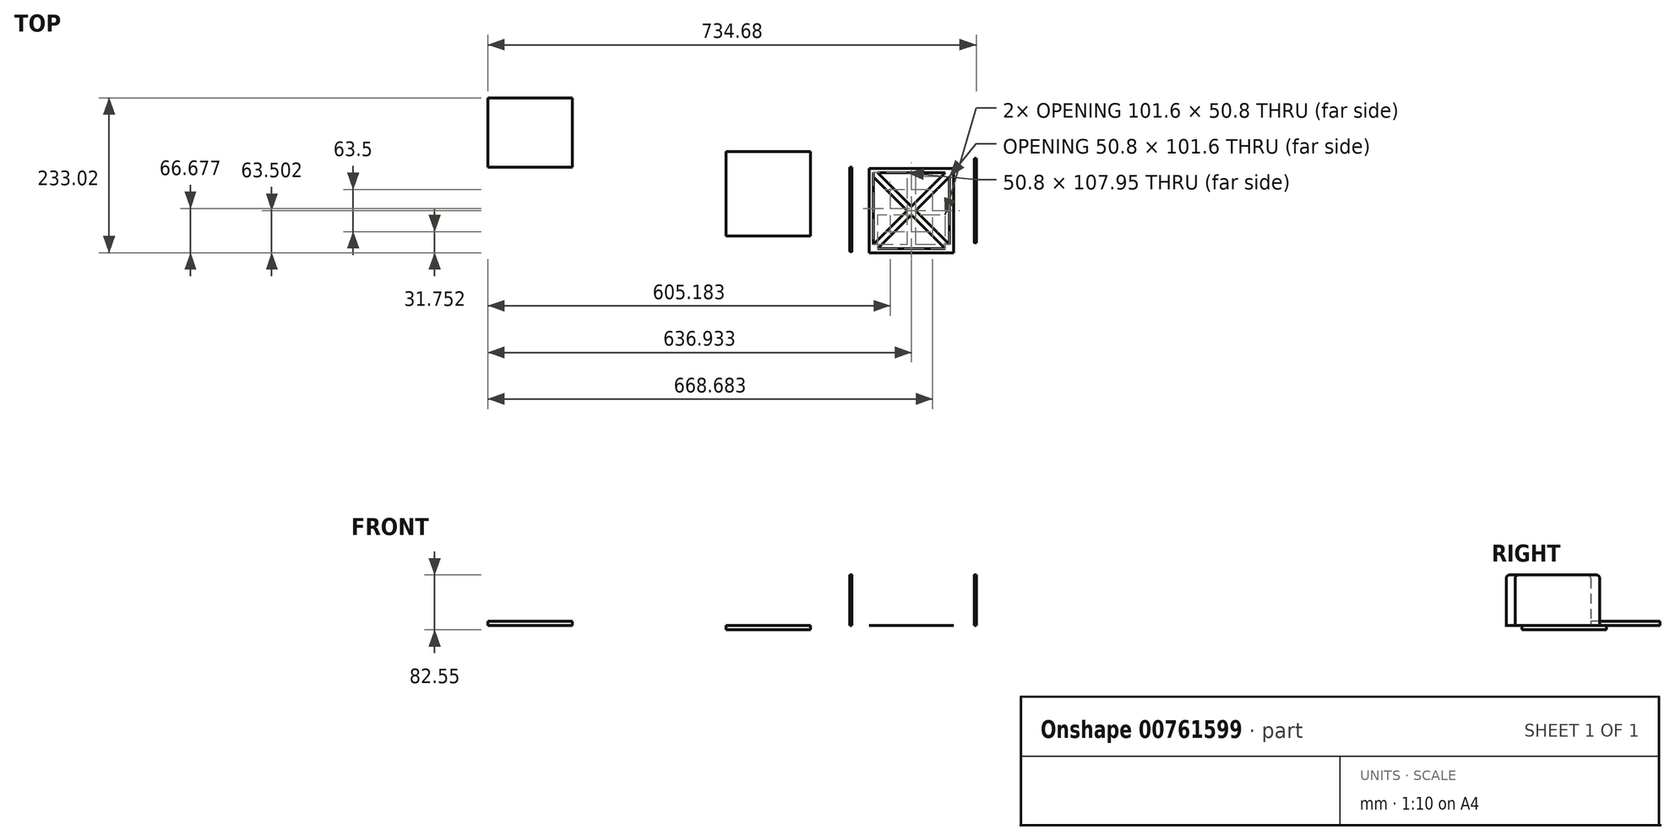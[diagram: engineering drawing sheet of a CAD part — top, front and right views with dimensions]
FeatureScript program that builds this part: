
annotation { "Feature Type Name" : "Feature", "Feature Type Description" : "" }
export const myFeature = defineFeature(function(context is Context, id is Id, definition is map)
    precondition{}
    {
        {
            var Q0;
            Q0=qCreatedBy(makeId("Top.planeOp"),FACE);
            var sketch = newSketch(context, id + "F0", { "sketchPlane" : qUnion([Q0])});
            skLineSegment(sketch, "E0.bottom", {"start": v(-34.56, 29.71) * mm, "end": v(79.74, 29.71) * mm});
            skLineSegment(sketch, "E0.top", {"start": v(-34.56, -84.59) * mm, "end": v(79.74, -84.59) * mm});
            skLineSegment(sketch, "E0.left", {"start": v(-34.56, 29.71) * mm, "end": v(-34.56, -84.59) * mm});
            skLineSegment(sketch, "E0.right", {"start": v(79.74, 29.71) * mm, "end": v(79.74, -84.59) * mm});
            skLineSegment(sketch, "E1.bottom", {"start": v(79.74, 29.71) * mm, "end": v(79.74, 29.71) * mm});
            skLineSegment(sketch, "E1.top", {"start": v(79.74, -84.59) * mm, "end": v(79.74, -84.59) * mm});
            skLineSegment(sketch, "E2.bottom", {"start": v(79.74, 29.71) * mm, "end": v(86.1, 29.71) * mm});
            skLineSegment(sketch, "E2.top", {"start": v(79.74, -84.59) * mm, "end": v(86.1, -84.59) * mm});
            skLineSegment(sketch, "E2.right", {"start": v(86.1, 29.71) * mm, "end": v(86.1, -84.59) * mm});
            skLineSegment(sketch, "E3.bottom", {"start": v(-34.56, 29.71) * mm, "end": v(-40.9, 29.71) * mm});
            skLineSegment(sketch, "E3.top", {"start": v(-34.56, -84.59) * mm, "end": v(-40.9, -84.59) * mm});
            skLineSegment(sketch, "E3.right", {"start": v(-40.9, 29.71) * mm, "end": v(-40.9, -84.59) * mm});
            skLineSegment(sketch, "E4.left", {"start": v(-34.56, 29.71) * mm, "end": v(-34.55, 23.35) * mm});
            skLineSegment(sketch, "E5.bottom", {"start": v(-34.56, 29.71) * mm, "end": v(-28.2, 29.71) * mm});
            skLineSegment(sketch, "E5.top", {"start": v(-34.56, 23.36) * mm, "end": v(-28.2, 23.36) * mm});
            skLineSegment(sketch, "E5.left", {"start": v(-34.56, 29.71) * mm, "end": v(-34.56, 23.36) * mm});
            skLineSegment(sketch, "E5.right", {"start": v(-28.2, 29.71) * mm, "end": v(-28.2, 23.36) * mm});
            skLineSegment(sketch, "E6.bottom", {"start": v(79.74, -84.59) * mm, "end": v(73.4, -84.59) * mm});
            skLineSegment(sketch, "E6.top", {"start": v(79.74, -78.24) * mm, "end": v(73.4, -78.24) * mm});
            skLineSegment(sketch, "E6.left", {"start": v(79.74, -84.59) * mm, "end": v(79.74, -78.24) * mm});
            skLineSegment(sketch, "E6.right", {"start": v(73.4, -84.59) * mm, "end": v(73.4, -78.24) * mm});
            skLineSegment(sketch, "E7", {"start": v(-34.55, 23.35) * mm, "end": v(73.4, -84.59) * mm});
            skLineSegment(sketch, "E8", {"start": v(79.74, -78.24) * mm, "end": v(-28.2, 29.71) * mm});
            skLineSegment(sketch, "E9.bottom", {"start": v(-34.56, -84.59) * mm, "end": v(63.23, -84.59) * mm});
            skLineSegment(sketch, "E10.bottom", {"start": v(-40.9, -84.59) * mm, "end": v(86.1, -84.59) * mm});
            skLineSegment(sketch, "E10.top", {"start": v(-40.9, -90.94) * mm, "end": v(86.1, -90.94) * mm});
            skLineSegment(sketch, "E10.left", {"start": v(-40.9, -84.59) * mm, "end": v(-40.9, -90.94) * mm});
            skLineSegment(sketch, "E10.right", {"start": v(86.1, -84.59) * mm, "end": v(86.1, -90.94) * mm});
            skLineSegment(sketch, "E11.bottom", {"start": v(-40.9, 29.71) * mm, "end": v(86.1, 29.71) * mm});
            skLineSegment(sketch, "E11.top", {"start": v(-40.9, 29.71) * mm, "end": v(86.1, 29.71) * mm});
            skLineSegment(sketch, "E11.left", {"start": v(-40.9, 29.71) * mm, "end": v(-40.9, 29.71) * mm});
            skLineSegment(sketch, "E11.right", {"start": v(86.1, 29.71) * mm, "end": v(86.1, 29.71) * mm});
            skLineSegment(sketch, "E12.top", {"start": v(-40.9, 36.06) * mm, "end": v(86.1, 36.06) * mm});
            skLineSegment(sketch, "E12.left", {"start": v(-40.9, 29.71) * mm, "end": v(-40.9, 36.06) * mm});
            skLineSegment(sketch, "E12.right", {"start": v(86.1, 29.71) * mm, "end": v(86.1, 36.06) * mm});
            skLineSegment(sketch, "E13.bottom", {"start": v(-34.56, -84.59) * mm, "end": v(-28.2, -84.59) * mm});
            skLineSegment(sketch, "E13.top", {"start": v(-34.56, -78.24) * mm, "end": v(-28.2, -78.24) * mm});
            skLineSegment(sketch, "E13.left", {"start": v(-34.56, -84.59) * mm, "end": v(-34.56, -78.24) * mm});
            skLineSegment(sketch, "E13.right", {"start": v(-28.2, -84.59) * mm, "end": v(-28.2, -78.24) * mm});
            skLineSegment(sketch, "E14.bottom", {"start": v(79.74, 29.71) * mm, "end": v(73.4, 29.71) * mm});
            skLineSegment(sketch, "E14.top", {"start": v(79.74, 23.36) * mm, "end": v(73.4, 23.36) * mm});
            skLineSegment(sketch, "E14.left", {"start": v(79.74, 29.71) * mm, "end": v(79.74, 23.36) * mm});
            skLineSegment(sketch, "E14.right", {"start": v(73.4, 29.71) * mm, "end": v(73.4, 23.36) * mm});
            skLineSegment(sketch, "E15", {"start": v(-28.2, -84.59) * mm, "end": v(79.74, 23.36) * mm});
            skLineSegment(sketch, "E16", {"start": v(-34.56, -78.24) * mm, "end": v(73.4, 29.71) * mm});
            skSolve(sketch);
        }
        {
            var Q0;
            {var subQ3=sQuery(id+"F0.wireOp",EDGE,"E2.top");Q0=makeQuery(id+"F0.imprint","IMPRINT",FACE,{"disambiguationData":[TD([[makeQuery(id+"F0.imprint","IMPRINT",EDGE,{"derivedFrom":subQ3}),-1.0]])]});}
            var Q1;
            {var subQ5=sQuery(id+"F0.wireOp",EDGE,"E6.top");Q1=makeQuery(id+"F0.imprint","IMPRINT",FACE,{"disambiguationData":[TD([[makeQuery(id+"F0.imprint","IMPRINT",EDGE,{"derivedFrom":subQ5}),-1.0]])]});}
            var Q2;
            {var subQ4=sQuery(id+"F0.wireOp",EDGE,"E6.top");Q2=makeQuery(id+"F0.imprint","IMPRINT",FACE,{"disambiguationData":[TD([[makeQuery(id+"F0.imprint","IMPRINT",EDGE,{"derivedFrom":subQ4}),1.0]])]});}
            var Q3;
            {var subQ4=sQuery(id+"F0.wireOp",EDGE,"E13.top");Q3=makeQuery(id+"F0.imprint","IMPRINT",FACE,{"disambiguationData":[TD([[makeQuery(id+"F0.imprint","IMPRINT",EDGE,{"derivedFrom":subQ4}),-1.0]])]});}
            var Q4;
            {var subQ6=sQuery(id+"F0.wireOp",EDGE,"E13.top");Q4=makeQuery(id+"F0.imprint","IMPRINT",FACE,{"disambiguationData":[TD([[makeQuery(id+"F0.imprint","IMPRINT",EDGE,{"derivedFrom":subQ6}),1.0]])]});}
            var Q5;
            {var subQ5=sQuery(id+"F0.wireOp",EDGE,"E5.right");Q5=makeQuery(id+"F0.imprint","IMPRINT",FACE,{"disambiguationData":[TD([[makeQuery(id+"F0.imprint","IMPRINT",EDGE,{"derivedFrom":subQ5}),1.0]])]});}
            var Q6;
            {var subQ0=sQuery(id+"F0.wireOp",EDGE,"E15");var subQ1=sQuery(id+"F0.wireOp",EDGE,"E7");var subQ2=makeQuery(id+"F0.imprint","INTERSECT",VERTEX,{"derivedFrom":[subQ1,subQ0]});Q6=makeQuery(id+"F0.imprint","IMPRINT",FACE,{"disambiguationData":[TD([[makeQuery(id+"F0.imprint","IMPRINT",EDGE,{"disambiguationData":[TD([[subQ2,1.0]])],"derivedFrom":subQ1}),1.0]])]});}
            var Q7;
            {var subQ1=sQuery(id+"F0.wireOp",EDGE,"E14.top");Q7=makeQuery(id+"F0.imprint","IMPRINT",FACE,{"disambiguationData":[TD([[makeQuery(id+"F0.imprint","IMPRINT",EDGE,{"derivedFrom":subQ1}),1.0]])]});}
            var Q8;
            {var subQ4=sQuery(id+"F0.wireOp",EDGE,"E14.top");Q8=makeQuery(id+"F0.imprint","IMPRINT",FACE,{"disambiguationData":[TD([[makeQuery(id+"F0.imprint","IMPRINT",EDGE,{"derivedFrom":subQ4}),-1.0]])]});}
            var Q9;
            {var subQ0=sQuery(id+"F0.wireOp",EDGE,"E5.right");Q9=makeQuery(id+"F0.imprint","IMPRINT",FACE,{"disambiguationData":[TD([[makeQuery(id+"F0.imprint","IMPRINT",EDGE,{"derivedFrom":subQ0}),-1.0]])]});}
            var Q10;
            {var subQ0=sQuery(id+"F0.wireOp",EDGE,"E2.bottom");Q10=makeQuery(id+"F0.imprint","IMPRINT",FACE,{"disambiguationData":[TD([[makeQuery(id+"F0.imprint","IMPRINT",EDGE,{"derivedFrom":subQ0}),1.0]])]});}
            var Q11;
            {var subQ0=sQuery(id+"F0.wireOp",EDGE,"E3.bottom");Q11=makeQuery(id+"F0.imprint","IMPRINT",FACE,{"disambiguationData":[TD([[makeQuery(id+"F0.imprint","IMPRINT",EDGE,{"derivedFrom":subQ0}),1.0]])]});}
            var Q12;
            {var subQ0=sQuery(id+"F0.wireOp",EDGE,"E2.bottom");Q12=makeQuery(id+"F0.imprint","IMPRINT",FACE,{"disambiguationData":[TD([[makeQuery(id+"F0.imprint","IMPRINT",EDGE,{"derivedFrom":subQ0}),-1.0]])]});}
            extrude(context, id + "F1", {"entities" : qUnion([Q0, Q1, Q2, Q3, Q4, Q5, Q6, Q7, Q8, Q9, Q10, Q11, Q12]), "depth" : 1 / 203.2 * mm, "offsetDistance" : 25.4 * mm});
        }
        {
            var Q0;
            Q0=qCreatedBy(makeId("Top.planeOp"),FACE);
            var sketch = newSketch(context, id + "F2", { "sketchPlane" : qUnion([Q0])});
            skLineSegment(sketch, "E17.bottom", {"start": v(-70.06, 37.76) * mm, "end": v(-66.88, 37.76) * mm});
            skLineSegment(sketch, "E17.top", {"start": v(-70.06, -89.24) * mm, "end": v(-66.88, -89.24) * mm});
            skLineSegment(sketch, "E17.left", {"start": v(-70.06, 37.76) * mm, "end": v(-70.06, -89.24) * mm});
            skLineSegment(sketch, "E17.right", {"start": v(-66.88, 37.76) * mm, "end": v(-66.88, -89.24) * mm});
            skSolve(sketch);
        }
        {
            var Q0;
            Q0=makeQuery(id+"F2.imprint","IMPRINT",FACE,{"disambiguationData":[TD([[makeQuery(id+"F2.imprint","IMPRINT",EDGE,{"derivedFrom":sQuery(id+"F2.wireOp",EDGE,"E17.bottom")}),-1.0]])]});
            extrude(context, id + "F3", {"entities" : qUnion([Q0]), "depth" : 76.2 * mm, "offsetDistance" : 25.4 * mm});
        }
        {
            var Q0;
            Q0=qCreatedBy(makeId("Top.planeOp"),FACE);
            var sketch = newSketch(context, id + "F4", { "sketchPlane" : qUnion([Q0])});
            skLineSegment(sketch, "E18.bottom", {"start": v(117.16, 51.25) * mm, "end": v(120.34, 51.25) * mm});
            skLineSegment(sketch, "E18.top", {"start": v(117.16, -75.75) * mm, "end": v(120.34, -75.75) * mm});
            skLineSegment(sketch, "E18.left", {"start": v(117.16, 51.25) * mm, "end": v(117.16, -75.75) * mm});
            skLineSegment(sketch, "E18.right", {"start": v(120.34, 51.25) * mm, "end": v(120.34, -75.75) * mm});
            skSolve(sketch);
        }
        {
            var Q0;
            Q0=makeQuery(id+"F4.imprint","IMPRINT",FACE,{"disambiguationData":[TD([[makeQuery(id+"F4.imprint","IMPRINT",EDGE,{"derivedFrom":sQuery(id+"F4.wireOp",EDGE,"E18.bottom")}),-1.0]])]});
            extrude(context, id + "F5", {"entities" : qUnion([Q0]), "depth" : 76.2 * mm, "offsetDistance" : 25.4 * mm});
        }
        {
            var Q0;
            Q0=qCreatedBy(makeId("Top.planeOp"),FACE);
            var sketch = newSketch(context, id + "F6", { "sketchPlane" : qUnion([Q0])});
            skLineSegment(sketch, "E19.bottom", {"start": v(-255.94, 61.3) * mm, "end": v(-128.94, 61.3) * mm});
            skLineSegment(sketch, "E19.top", {"start": v(-255.94, -65.7) * mm, "end": v(-128.94, -65.7) * mm});
            skLineSegment(sketch, "E19.left", {"start": v(-255.94, 61.3) * mm, "end": v(-255.94, -65.7) * mm});
            skLineSegment(sketch, "E19.right", {"start": v(-128.94, 61.3) * mm, "end": v(-128.94, -65.7) * mm});
            skSolve(sketch);
        }
        {
            var Q0;
            Q0=makeQuery(id+"F6.imprint","IMPRINT",FACE,{"disambiguationData":[TD([[makeQuery(id+"F6.imprint","IMPRINT",EDGE,{"derivedFrom":sQuery(id+"F6.wireOp",EDGE,"E19.bottom")}),-1.0]])]});
            extrude(context, id + "F7", {"entities" : qUnion([Q0]), "oppositeDirection" : true, "depth" : 6.35 * mm, "offsetDistance" : 25.4 * mm});
        }
        {
            var Q0;
            Q0=makeQuery(id+"F3.opExtrude","CAP_EDGE",EDGE,{"disambiguationData":[OSD([sQuery(id+"F2.wireOp",EDGE,"E17.top")])],"isStart":false});
            fillet(context, id + "F8", {"entities" : qUnion([Q0]), "radius" : 5.08 * mm, "tangentPropagation" : true, "allowEdgeOverflow" : false});
        }
        {
            var Q0;
            Q0=makeQuery(id+"F3.opExtrude","CAP_EDGE",EDGE,{"disambiguationData":[OSD([sQuery(id+"F2.wireOp",EDGE,"E17.bottom")])],"isStart":false});
            fillet(context, id + "F9", {"entities" : qUnion([Q0]), "radius" : 5.08 * mm, "tangentPropagation" : true, "allowEdgeOverflow" : false});
        }
        {
            var Q0;
            Q0=makeQuery(id+"F5.opExtrude","CAP_EDGE",EDGE,{"disambiguationData":[OSD([sQuery(id+"F4.wireOp",EDGE,"E18.top")])],"isStart":false});
            fillet(context, id + "F10", {"entities" : qUnion([Q0]), "radius" : 5.08 * mm, "tangentPropagation" : true, "allowEdgeOverflow" : false});
        }
        {
            var Q0;
            Q0=makeQuery(id+"F5.opExtrude","CAP_EDGE",EDGE,{"disambiguationData":[OSD([sQuery(id+"F4.wireOp",EDGE,"E18.bottom")])],"isStart":false});
            fillet(context, id + "F11", {"entities" : qUnion([Q0]), "radius" : 5.08 * mm, "tangentPropagation" : true, "allowEdgeOverflow" : false});
        }
        {
            var Q0;
            Q0=qCreatedBy(makeId("Top.planeOp"),FACE);
            var sketch = newSketch(context, id + "F12", { "sketchPlane" : qUnion([Q0])});
            skLineSegment(sketch, "E20.bottom", {"start": v(-614.34, 142.08) * mm, "end": v(-487.34, 142.08) * mm});
            skLineSegment(sketch, "E20.top", {"start": v(-614.34, 37.94) * mm, "end": v(-487.34, 37.94) * mm});
            skLineSegment(sketch, "E20.left", {"start": v(-614.34, 142.08) * mm, "end": v(-614.34, 37.94) * mm});
            skLineSegment(sketch, "E20.right", {"start": v(-487.34, 142.08) * mm, "end": v(-487.34, 37.94) * mm});
            skSolve(sketch);
        }
        {
            var Q0;
            Q0=makeQuery(id+"F12.imprint","IMPRINT",FACE,{"disambiguationData":[TD([[makeQuery(id+"F12.imprint","IMPRINT",EDGE,{"derivedFrom":sQuery(id+"F12.wireOp",EDGE,"E20.bottom")}),-1.0]])]});
            extrude(context, id + "F13", {"entities" : qUnion([Q0]), "depth" : 6.35 * mm, "offsetDistance" : 25.4 * mm});
        }
    });
